# Revit family: LOROWERK 00320-150X
name_source: partatom
category: Rohrformteile
revit_build: Autodesk Revit 2017 (Build: 20160225_1515(x64)
units: mm (PartAtom-declared; Revit-internal decimal feet)

## family parameters
Arbeitsebenenbasiert = Nein
Beim Laden mit Abzugskörper schneiden = Nein
Bemaßung runder Anschluss = Durchmesser verwenden
Gemeinsam genutzt = Nein
Immer vertikal = Ja
Teiletyp = Bogen

## types (1)
- LOROWERK 00320-150X
    BIM = https://media.stage.bim.site
    Benennung = LORO-X Bogen 45°, DN150
    Beschreibung = LORO-X Stahlabflussrohre
    Bestellmenge (Multiplikator) = 1
    Brandschutzklasse = B1 nach DIN 4102
    CONNECTOR0_DIAMETER_dNBN0_0r = 150 mm
    CONNECTOR0_dNBN0_00 = 156 mm
    CONNECTOR0_dNBN0_01 = 71 mm
    CONNECTOR0_ref_dNBN0 = 71 mm
    CONNECTOR1_DIAMETER_dY_0r = 150 mm
    CONNECTOR1_dY_00 = 79 mm
    CONNECTOR1_dY_01 = 164 mm
    CONNECTOR1_ref_dY = 79 mm
    DATANORM = 00320.150X
    GTIN = 4038088019276
    HAN = 00320.150X
    Hersteller = LOROWERK K.H. Vahlbrauk GmbH & Co. KG
    Index = 5
    Ist System = Nein
    Ist Zubehör = Nein
    Nenndruck = 0.5
    Nenndrucksystem = PN
    Nennweitensystem = DN
    Normen/Regeln/Zulassungen = DVGW für Trinkwasser
    Produktbezeichnung = LORO-X Stahlabflussrohre
    Produktkennung = Formstück
    Produktname = LORO-X Bogen 45°
    Produktvideo = https://media.stage.bim.site
    Querschnittsform = rund
    Typname = LORO-X Bogen 45°
    VDIBSN = 020001???001001???00100100000100300700000000000090000000000000000005
    Verbindungsart I = Pressen
    Verbindungsart II = axial pressen
    Verlegeart = unter Putz
    max. zul. Dauer-Betriebstemperatur [Kelvin] = 95
